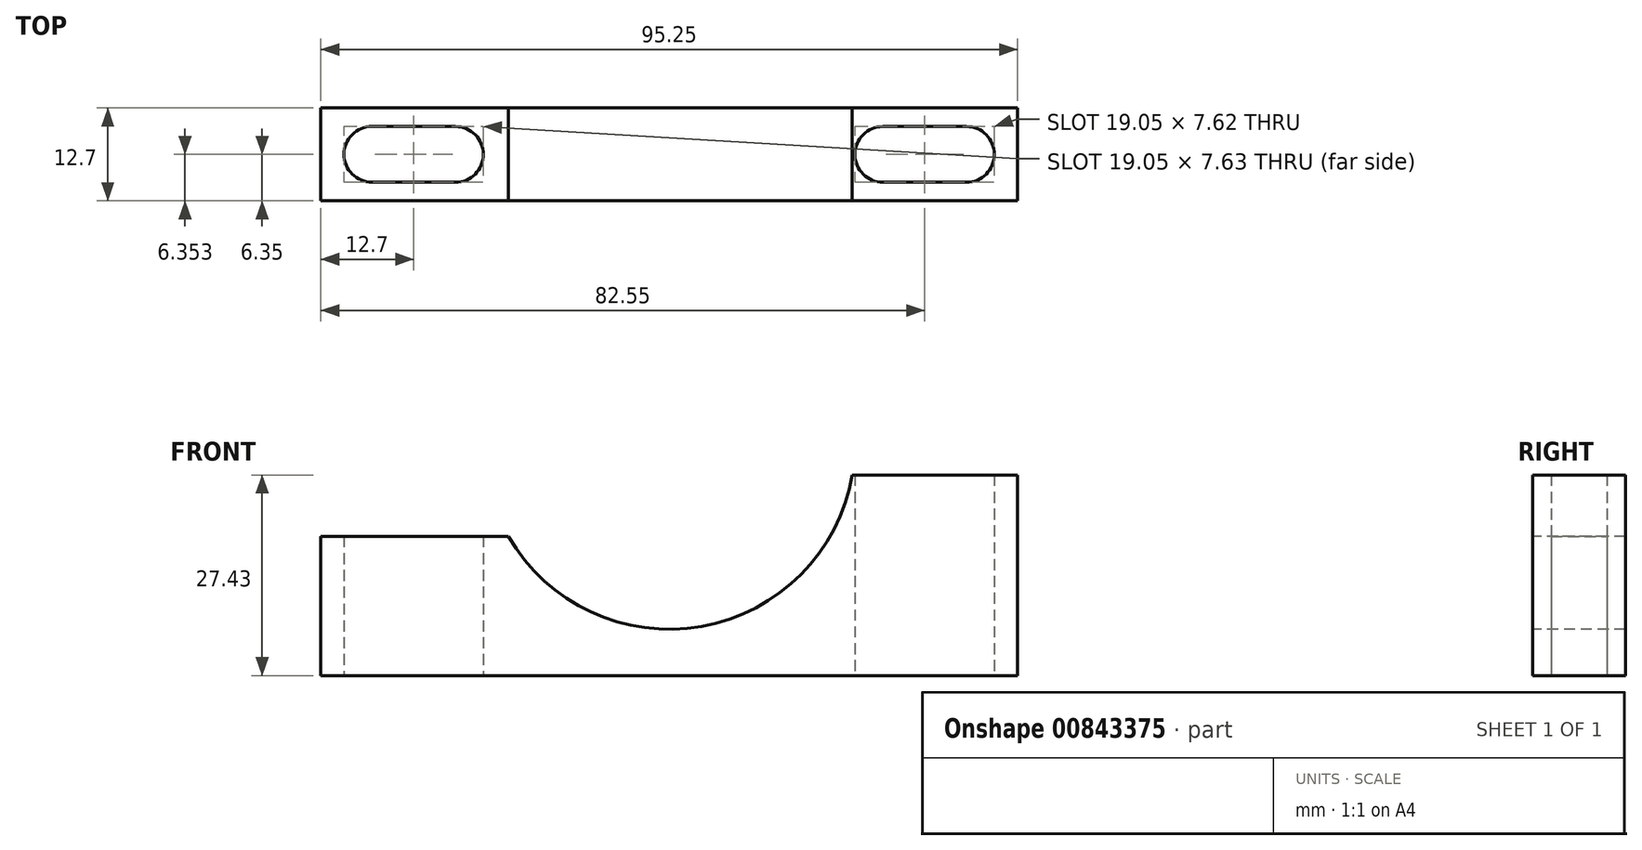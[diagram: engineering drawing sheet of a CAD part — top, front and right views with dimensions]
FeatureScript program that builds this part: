
annotation { "Feature Type Name" : "Feature", "Feature Type Description" : "" }
export const myFeature = defineFeature(function(context is Context, id is Id, definition is map)
    precondition{}
    {
        {
            var Q0;
            Q0=qCreatedBy(makeId("Front.planeOp"),FACE);
            var sketch = newSketch(context, id + "F0", { "sketchPlane" : qUnion([Q0])});
            skLineSegment(sketch, "E0", {"start": v(0, 0) * mm, "end": v(95.25, 0) * mm});
            skLineSegment(sketch, "E1", {"start": v(0, 0) * mm, "end": v(0, 19.05) * mm});
            skLineSegment(sketch, "E2", {"start": v(0, 19.05) * mm, "end": v(95.25, 19.05) * mm});
            skLineSegment(sketch, "E3", {"start": v(95.25, 19.05) * mm, "end": v(95.25, 0) * mm});
            skSolve(sketch);
        }
        {
            var Q0;
            Q0=makeQuery(id+"F0.imprint","IMPRINT",FACE,{"disambiguationData":[TD([[makeQuery(id+"F0.imprint","IMPRINT",EDGE,{"derivedFrom":sQuery(id+"F0.wireOp",EDGE,"E0")}),1.0]])]});
            extrude(context, id + "F1", {"entities" : qUnion([Q0]), "depth" : 12.7 * mm, "offsetDistance" : 25.4 * mm});
        }
        {
            var Q0;
            Q0=makeQuery(id+"F1.opExtrude","SWEPT_FACE",FACE,{"disambiguationData":[OSD([sQuery(id+"F0.wireOp",EDGE,"E0")])]});
            var sketch = newSketch(context, id + "F2", { "sketchPlane" : qUnion([Q0])});
            skArc(sketch, "E4", {"start": v(6.98, 10.15) * mm, "mid": v(3.17, 6.34) * mm, "end": v(6.99, 2.53) * mm});
            skArc(sketch, "E5", {"start": v(88.27, 2.54) * mm, "mid": v(92.08, 6.35) * mm, "end": v(88.27, 10.16) * mm});
            skArc(sketch, "E6", {"start": v(76.83, 10.16) * mm, "mid": v(73.03, 6.35) * mm, "end": v(76.83, 2.54) * mm});
            skLineSegment(sketch, "E7", {"start": v(76.83, 10.16) * mm, "end": v(88.27, 10.16) * mm});
            skLineSegment(sketch, "E8", {"start": v(76.83, 2.54) * mm, "end": v(88.27, 2.54) * mm});
            skArc(sketch, "E9", {"start": v(18.42, 2.54) * mm, "mid": v(22.22, 6.35) * mm, "end": v(18.41, 10.16) * mm});
            skLineSegment(sketch, "E10", {"start": v(6.98, 10.15) * mm, "end": v(18.41, 10.16) * mm});
            skLineSegment(sketch, "E11", {"start": v(18.42, 2.54) * mm, "end": v(6.99, 2.53) * mm});
            skSolve(sketch);
        }
        {
            var Q0;
            Q0=makeQuery(id+"F2.imprint","IMPRINT",FACE,{"disambiguationData":[TD([[makeQuery(id+"F2.imprint","IMPRINT",EDGE,{"derivedFrom":sQuery(id+"F2.wireOp",EDGE,"E4")}),1.0]])]});
            var Q1;
            Q1=makeQuery(id+"F2.imprint","IMPRINT",FACE,{"disambiguationData":[TD([[makeQuery(id+"F2.imprint","IMPRINT",EDGE,{"derivedFrom":sQuery(id+"F2.wireOp",EDGE,"E5")}),1.0]])]});
            extrude(context, id + "F3", {"entities" : qUnion([Q0, Q1]), "operationType" : NewBodyOperationType.REMOVE, "endBound" : BoundingType.THROUGH_ALL, "oppositeDirection" : true, "depth" : 25.4 * mm, "offsetDistance" : 25.4 * mm});
        }
        {
            var Q0;
            {var subQ0=sQuery(id+"F0.wireOp",EDGE,"E3");var subQ1=sQuery(id+"F0.wireOp",EDGE,"E2");Q0=makeQuery(id+"Fio1kGih3YMk8nf_1.boolean.opBoolean","SPLIT",FACE,{"disambiguationData":[TD([makeQuery(id+"F1.opExtrude","SWEPT_FACE",FACE,{"disambiguationData":[OSD([subQ0])]})])],"derivedFrom":makeQuery(id+"F1.opExtrude","SWEPT_FACE",FACE,{"disambiguationData":[OSD([subQ1])]})});}
            var sketch = newSketch(context, id + "F4", { "sketchPlane" : qUnion([Q0])});
            skLineSegment(sketch, "E12", {"start": v(69.62, 0) * mm, "end": v(95.25, 0) * mm});
            skLineSegment(sketch, "E13", {"start": v(95.25, 0) * mm, "end": v(95.25, -12.7) * mm});
            skLineSegment(sketch, "E14", {"start": v(95.25, -12.7) * mm, "end": v(69.62, -12.7) * mm});
            skLineSegment(sketch, "E15", {"start": v(69.62, -12.7) * mm, "end": v(69.62, 0) * mm});
            skSolve(sketch);
        }
        {
            var Q0;
            Q0=makeQuery(id+"F4.imprint","IMPRINT",FACE,{"disambiguationData":[TD([[makeQuery(id+"F4.imprint","IMPRINT",EDGE,{"derivedFrom":sQuery(id+"F4.wireOp",EDGE,"E12")}),-1.0]])]});
            extrude(context, id + "F5", {"entities" : qUnion([Q0]), "operationType" : NewBodyOperationType.ADD, "depth" : 8.38 * mm, "offsetDistance" : 25.4 * mm});
        }
        {
            var Q0;
            Q0=makeQuery(id+"F5.boolean.opBoolean","MERGE",FACE,{"derivedFrom":[makeQuery(id+"F1.opExtrude","CAP_FACE",FACE,{"disambiguationData":[OSD([sQuery(id+"F0.wireOp",EDGE,"E0"),sQuery(id+"F0.wireOp",EDGE,"E1"),sQuery(id+"F0.wireOp",EDGE,"E2"),sQuery(id+"F0.wireOp",EDGE,"E3")])],"isStart":false}),makeQuery(id+"F5.opExtrude","SWEPT_FACE",FACE,{"disambiguationData":[OSD([sQuery(id+"F4.wireOp",EDGE,"E14")])]})]});
            var sketch = newSketch(context, id + "F6", { "sketchPlane" : qUnion([Q0])});
            skLineSegment(sketch, "E16", {"start": v(0, 19.05) * mm, "end": v(95.25, 19.05) * mm});
            skPoint(sketch, "E16.endSnap0", {"position": v(95.25, 13.72) * mm});
            skCircle(sketch, "E17", {"center": v(47.63, 31.75) * mm, "radius": 25.4 * mm});
            skSolve(sketch);
        }
        {
            var Q0;
            {var subQ0=sQuery(id+"F6.wireOp",EDGE,"E17");var subQ1=sQuery(id+"F6.wireOp",EDGE,"E16");var subQ3=makeQuery(id+"F6.imprint","INTERSECT",VERTEX,{"derivedFrom":[subQ1,subQ0]});Q0=makeQuery(id+"F6.imprint","IMPRINT",FACE,{"disambiguationData":[TD([[makeQuery(id+"F6.imprint","IMPRINT",EDGE,{"disambiguationData":[TD([[subQ3,-1.0]])],"derivedFrom":subQ1}),-1.0]])]});}
            var Q1;
            {var subQ1=sQuery(id+"F4.wireOp",EDGE,"E14");var subQ2=makeQuery(id+"F5.opExtrude","SWEPT_EDGE",EDGE,{"disambiguationData":[OSD([sQuery(id+"F0.wireOp",EDGE,"E2"),subQ1,sQuery(id+"F4.wireOp",EDGE,"E15")])]});Q1=makeQuery(id+"F6.imprint","IMPRINT",FACE,{"disambiguationData":[TD([[makeQuery(id+"F6.imprint","IMPRINT",EDGE,{"derivedFrom":subQ2}),1.0]])]});}
            extrude(context, id + "F7", {"entities" : qUnion([Q0, Q1]), "operationType" : NewBodyOperationType.REMOVE, "endBound" : BoundingType.THROUGH_ALL, "oppositeDirection" : true, "depth" : 25.4 * mm, "offsetDistance" : 25.4 * mm});
        }
    });
